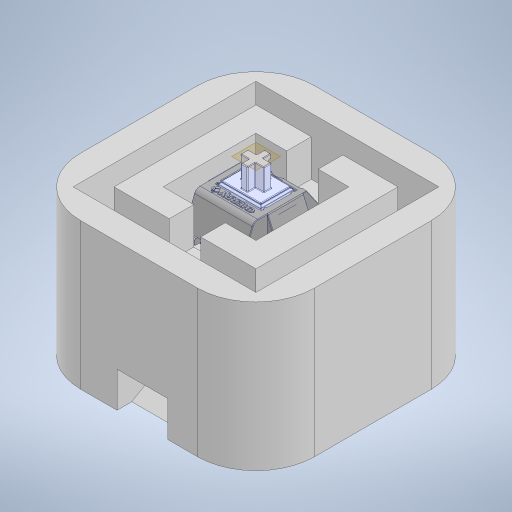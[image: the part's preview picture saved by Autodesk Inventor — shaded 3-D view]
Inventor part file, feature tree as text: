
AUTODESK INVENTOR PART (.ipt)
format: ipt  version: 2023 (Build 270158000, 158)  size: 2,576,896 bytes
history: native  units: in
note: dims shown in document units (in); Inventor stores cm internally (conversion verified against a paired STEP export)
features: extrude x8, other x7, plane x4, sketch x4, fillet x2, projected_geometry x2, chamfer x1, boolean_combine x1
ambient origin geometry x8: Origin, YZ Plane, XZ Plane, XY Plane, X Axis, Y Axis, Z Axis, Center Point
bodies: Solid1 (feature_tree), Solid7 (feature_tree), Solid8 (feature_tree), Solid9 (feature_tree), Solid10 (feature_tree)
feature tree (29):
  plane  "Work Plane1"
  sketch  "Sketch3"  dims[d11=0.0118in d15=0.1969in d16=0.0in]
  extrude  "Extrusion3"  Depth=0.1969in TaperAngle=0.0deg
  extrude  "Extrusion5"  Depth=1.5748in
  extrude  "Extrusion6"  Depth=0.3937in TaperAngle=0.0deg
  plane  "Work Plane2"
  sketch  "Sketch4"  dims[d19=0.1417in d20=0.0in d21=1.5748in]
  extrude  "Extrusion7"  Depth=0.0787in TaperAngle=0.0deg
  extrude  "Extrusion8"  Depth=0.3937in TaperAngle=0.0deg
  plane  "Work Plane3"
  extrude  "Extrusion9"  Depth=0.0787in
  plane  "Work Plane4"
  extrude  "Extrusion10"  Depth=0.0787in
  fillet  "Fillet1"  [1 undecoded]
  chamfer  "Chamfer2"  Distance=0.0059in
  extrude  "Extrusion11"  Depth=0.0787in
  fillet  "Fillet2"  Radius=0.0039in
  boolean_combine  "Combine1"
  projected_geometry  "Projected Loop3"
  other  "lid"
  projected_geometry  "Projected Loop5"
  other  "bottom"
  sketch  "Sketch7"  dims[d22=1.5748in d34=0.3937in d35=0.0in]
  sketch  "Sketch8"  dims[d36=-2.4737in d37=0.9843in d38=0.0in d48=0.3937in d49=0.0in d50=0.0059in d51=0.0059in d52=0.0in d53=0.0059in d55=0.0039in d57=0.0039in d58=0.0079in d59=0.0039in d60=0.0059in d61=0.6201in d62=0.0in d63=0.0in d64=30.0deg d66=0.4434in d67=0.7842in d68=0.0in d69=0.0in d70=0.3937in d71=0.0184in d72=0.0787in d73=45.0deg d74=0.1811in d75=0.1811in d76=0.1811in d77=0.1811in d78=0.1063in d79=0.0098in d80=0.0098in d81=0.0098in d82=0.0098in d83=0.1378in d84=0.248in d85=0.0in d86=0.0787in d87=0.0035in d17=0.0197in d18=0.0344in]
  other  "MX-solid1-F1"
  other  "MX-solid6-F6"
  other  "T-2-solid1"
  other  "T-2-solid2"
  other  "Boss-Extrude1"
note: 1 required parameter value undecoded (feature->parameter linkage not recoverable at this tier; creation-order binding heuristic only, values carry confidence <= 0.55)
